# Revit family: 16.1 Настенный осевой вентилятор FE Тип В
name_source: partatom
category: Оборудование
revit_build: Autodesk Revit 2016 (Build: 20151209_0715(x64)
units: mm (PartAtom-declared; Revit-internal decimal feet)

## family parameters
Всегда вертикально = Да
На основе рабочей плоскости = Нет
Общий = Нет
При загрузке вырезать с полостями = Нет
Размер круглого соединителя = Использовать диаметр
Тип детали = Нормальный
Точка расчета площади = Нет

## types (13) — shared parameters
R скругления = 15 мм
Единица измерения = шт.
Завод изготовитель = KORF
Ключевая пометка = Вентиляция
Материал = Сталь серая
Наименование и тех.хар-ка = Настенный осевой вентилятор
Раздел = ОВ
отступ = 32 мм

## per-type parameters (varying)
| type | D | D1 | D2 | d | d1 | d2 | А | Б | Г | Д | Е | Ж | И | К | Масса единицы | Мощность, кВт | Размер В | Сила тока J, А | Тип, марка, обозначение | Частота вращения n, об/мин |
| FE040-VDQ | 462 мм | 210 мм | 126 мм | 143 мм | 210 мм | 378 мм | 490 мм | 540 мм | 420 мм | 378 мм | 139 мм | 86 мм | 88 мм | 178 мм | 8,5 кг | 0 Вт | 9 мм | 0.48 | FE040-VDQ.2С.A7 | 1300 |
| FE040-4EQ | 462 мм | 210 мм | 126 мм | 143 мм | 210 мм | 378 мм | 490 мм | 540 мм | 420 мм | 378 мм | 154 мм | 86 мм | 88 мм | 193 мм | 10.2 кг | 0 Вт | 9 мм | 1.35 | FE040-4EQ.2F.A7 | 1320 |
| FE045-VDQ | 528 мм | 240 мм | 144 мм | 163 мм | 240 мм | 432 мм | 535 мм | 575 мм | 480 мм | 432 мм | 186 мм | 92 мм | 96 мм | 198 мм | 13.6 кг | 1 Вт | 11 мм | 1.15 | FE045-VDQ.4F.A7 | 1340 |
| FE045-4EQ | 528 мм | 240 мм | 144 мм | 163 мм | 240 мм | 432 мм | 535 мм | 575 мм | 480 мм | 432 мм | 206 мм | 92 мм | 96 мм | 218 мм | 15.1 кг | 1 Вт | 11 мм | 2.8 | FE045-4EQ.4I.A7 | 1310 |
| FE050-VDQ | 581 мм | 264 мм | 158 мм | 180 мм | 264 мм | 475 мм | 615 мм | 655 мм | 528 мм | 475 мм | 206 мм | 105 мм | 104 мм | 218 мм | 19.2 кг | 1 Вт | 11 мм | 1.35 | FE050-VDQ.4I.A7 | 1340 |
| FE050-4EQ | 581 мм | 264 мм | 158 мм | 180 мм | 264 мм | 475 мм | 615 мм | 655 мм | 528 мм | 475 мм | 206 мм | 105 мм | 104 мм | 218 мм | 19.2 кг | 1 Вт | 11 мм | 3.4 | FE050-4EQ.4I.A7 | 1210 |
| FE050-SDQ | 581 мм | 264 мм | 158 мм | 180 мм | 264 мм | 475 мм | 615 мм | 655 мм | 528 мм | 475 мм | 186 мм | 105 мм | 104 мм | 198 мм | 17 кг | 0 Вт | 11 мм | 0.74 | FE050-SDQ.4F.A7 | 900 |
| FE056-6EQ | 581 мм | 264 мм | 158 мм | 180 мм | 264 мм | 475 мм | 615 мм | 655 мм | 528 мм | 475 мм | 186 мм | 105 мм | 104 мм | 198 мм | 17 кг | 0 Вт | 11 мм | 1.25 | FE056-6EQ.4M.A7 | 890 |
| FE056-VDQ | 648 мм | 295 мм | 177 мм | 200 мм | 295 мм | 530 мм | 675 мм | 725 мм | 589 мм | 530 мм | 226 мм | 116 мм | 119 мм | 238 мм | 25 кг | 1 Вт | 11 мм | 2.6 | FE056-VDQ.4F.A7 | 1320 |
| FE056-SDQ | 648 мм | 295 мм | 177 мм | 200 мм | 295 мм | 530 мм | 675 мм | 725 мм | 589 мм | 530 мм | 186 мм | 116 мм | 119 мм | 198 мм | 21 кг | 0 Вт | 11 мм | 0.76 | FE056-SDQ.4I.A7 | 880 |
| FE056-6EQ.4M | 648 мм | 295 мм | 177 мм | 200 мм | 295 мм | 530 мм | 675 мм | 725 мм | 589 мм | 530 мм | 206 мм | 116 мм | 119 мм | 218 мм | 23 кг | 1 Вт | 11 мм | 2.3 | FE056-6EQ.4M.A7 | 920 |
| FE063-SDQ | 730 мм | 332 мм | 199 мм | 226 мм | 332 мм | 598 мм | 750 мм | 805 мм | 664 мм | 598 мм | 206 мм | 129 мм | 130 мм | 219 мм | 25.5 кг | 1 Вт | 11 мм | 1.25 | FE063-SDQ.4I.A7 | 900 |
| FE063-6EQ | 730 мм | 332 мм | 199 мм | 226 мм | 332 мм | 598 мм | 750 мм | 805 мм | 664 мм | 598 мм | 225 мм | 129 мм | 130 мм | 238 мм | 27.5 кг | 1 Вт | 11 мм | 3.5 | FE063-6EQ.4M.A7 | 900 |
